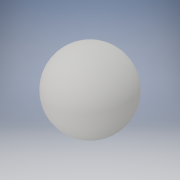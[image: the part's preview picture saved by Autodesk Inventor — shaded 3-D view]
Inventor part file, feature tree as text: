
AUTODESK INVENTOR PART (.ipt)
format: ipt  version: 2018 (Build 220112000, 112)  size: 126,976 bytes
history: native  units: in
note: dims shown in document units (in); Inventor stores cm internally (conversion verified against a paired STEP export)
features: revolve x1, sketch x1
ambient origin geometry x8: Origin, YZ Plane, XZ Plane, XY Plane, X Axis, Y Axis, Z Axis, Center Point
bodies: Solid1 (feature_tree)
feature tree (2):
  revolve  "Revolution1"  Angle=90.0deg
  sketch  "Sketch1"  dims[d0=13.0in d1=90.0deg]
